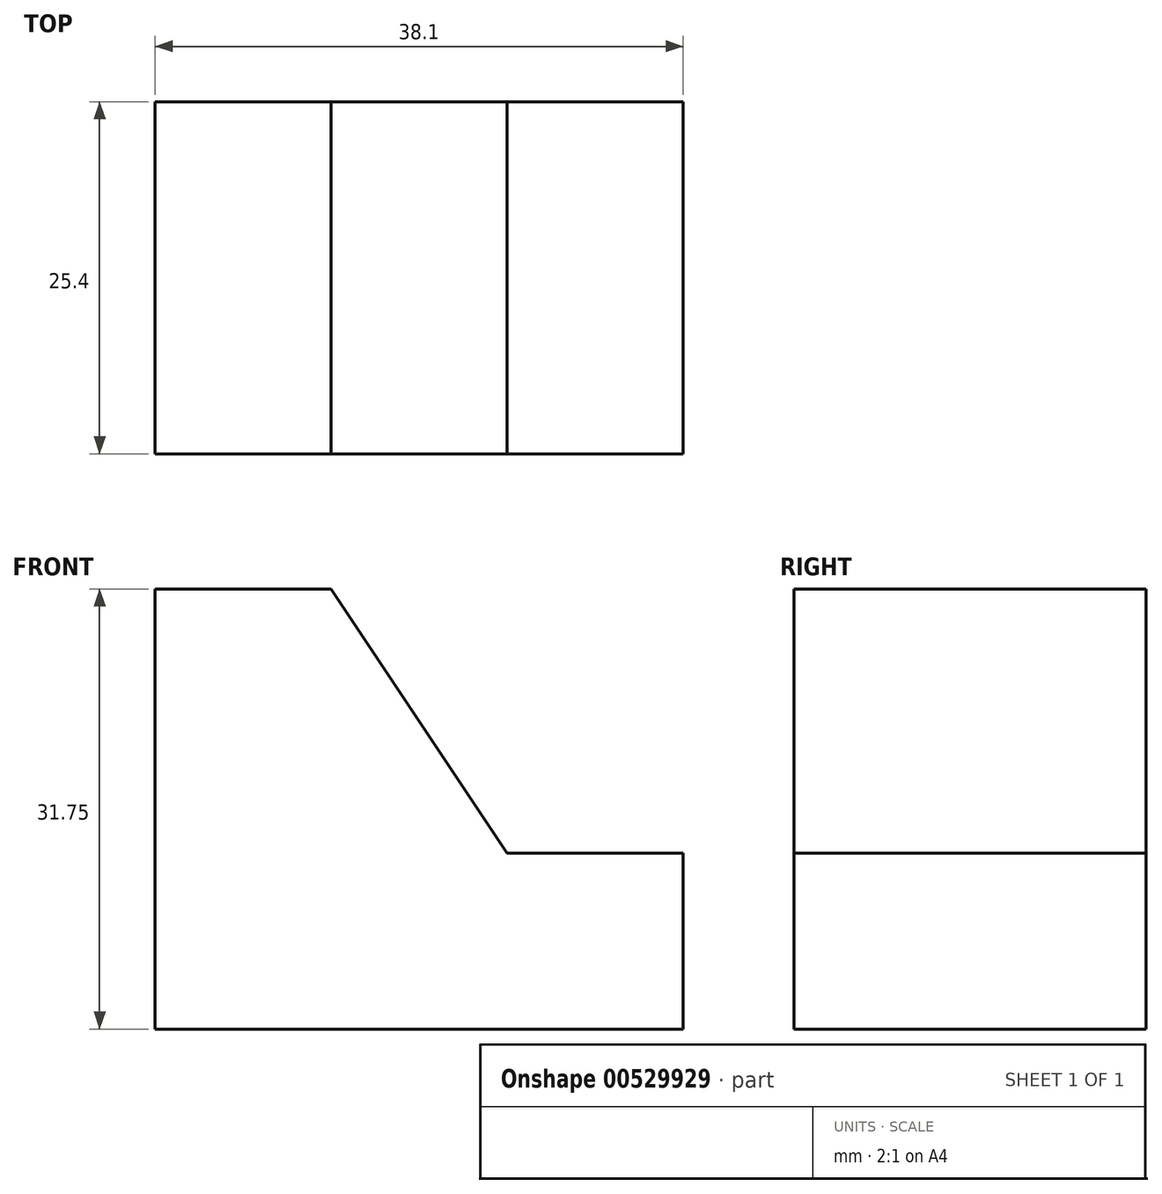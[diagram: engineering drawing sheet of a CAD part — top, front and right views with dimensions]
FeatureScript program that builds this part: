
annotation { "Feature Type Name" : "Feature", "Feature Type Description" : "" }
export const myFeature = defineFeature(function(context is Context, id is Id, definition is map)
    precondition{}
    {
        {
            var Q0;
            Q0=qCreatedBy(makeId("Front.planeOp"),FACE);
            var sketch = newSketch(context, id + "F0", { "sketchPlane" : qUnion([Q0])});
            skLineSegment(sketch, "E0", {"start": v(2.57, 49.39) * mm, "end": v(2.57, 17.64) * mm});
            skLineSegment(sketch, "E1", {"start": v(2.57, 17.64) * mm, "end": v(40.67, 17.64) * mm});
            skLineSegment(sketch, "E2", {"start": v(40.67, 17.64) * mm, "end": v(40.67, 30.34) * mm});
            skLineSegment(sketch, "E3", {"start": v(40.67, 30.34) * mm, "end": v(27.97, 30.34) * mm});
            skLineSegment(sketch, "E4", {"start": v(27.97, 30.34) * mm, "end": v(15.27, 49.39) * mm});
            skLineSegment(sketch, "E5", {"start": v(15.27, 49.39) * mm, "end": v(2.57, 49.39) * mm});
            skSolve(sketch);
        }
        {
            var Q0;
            Q0=makeQuery(id+"F0.imprint","IMPRINT",FACE,{"disambiguationData":[TD([[makeQuery(id+"F0.imprint","IMPRINT",EDGE,{"derivedFrom":sQuery(id+"F0.wireOp",EDGE,"E0")}),1.0]])]});
            extrude(context, id + "F1", {"entities" : qUnion([Q0]), "depth" : 25.4 * mm, "offsetDistance" : 25.4 * mm});
        }
    });
